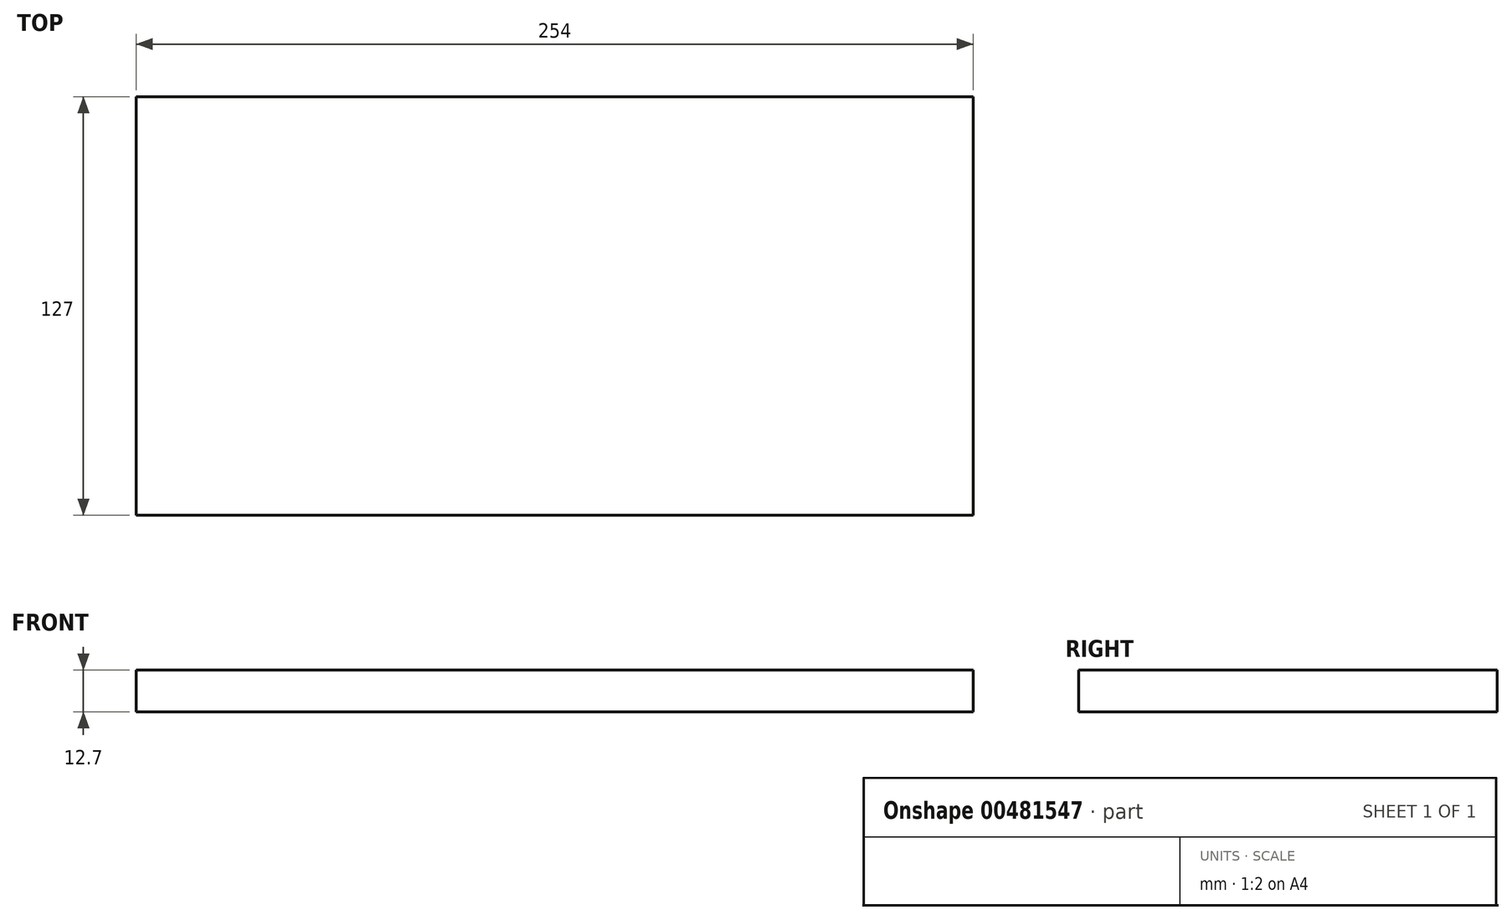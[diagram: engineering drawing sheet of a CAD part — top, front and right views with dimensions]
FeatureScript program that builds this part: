
annotation { "Feature Type Name" : "Feature", "Feature Type Description" : "" }
export const myFeature = defineFeature(function(context is Context, id is Id, definition is map)
    precondition{}
    {
        {
            var Q0;
            Q0=qCreatedBy(makeId("Top.planeOp"),FACE);
            var sketch = newSketch(context, id + "F0", { "sketchPlane" : qUnion([Q0])});
            skLineSegment(sketch, "E0.bottom", {"start": v(-127, 63.5) * mm, "end": v(127, 63.5) * mm});
            skLineSegment(sketch, "E0.top", {"start": v(-127, -63.5) * mm, "end": v(127, -63.5) * mm});
            skLineSegment(sketch, "E0.left", {"start": v(-127, 63.5) * mm, "end": v(-127, -63.5) * mm});
            skLineSegment(sketch, "E0.right", {"start": v(127, 63.5) * mm, "end": v(127, -63.5) * mm});
            skPoint(sketch, "E0.middle", {"position": v(0, 0) * mm});
            skSolve(sketch);
        }
        {
            var Q0;
            Q0 = qSketchRegion(id + "F0", true);
            extrude(context, id + "F1", {"entities" : qUnion([Q0]), "depth" : 12.7 * mm});
        }
    });
